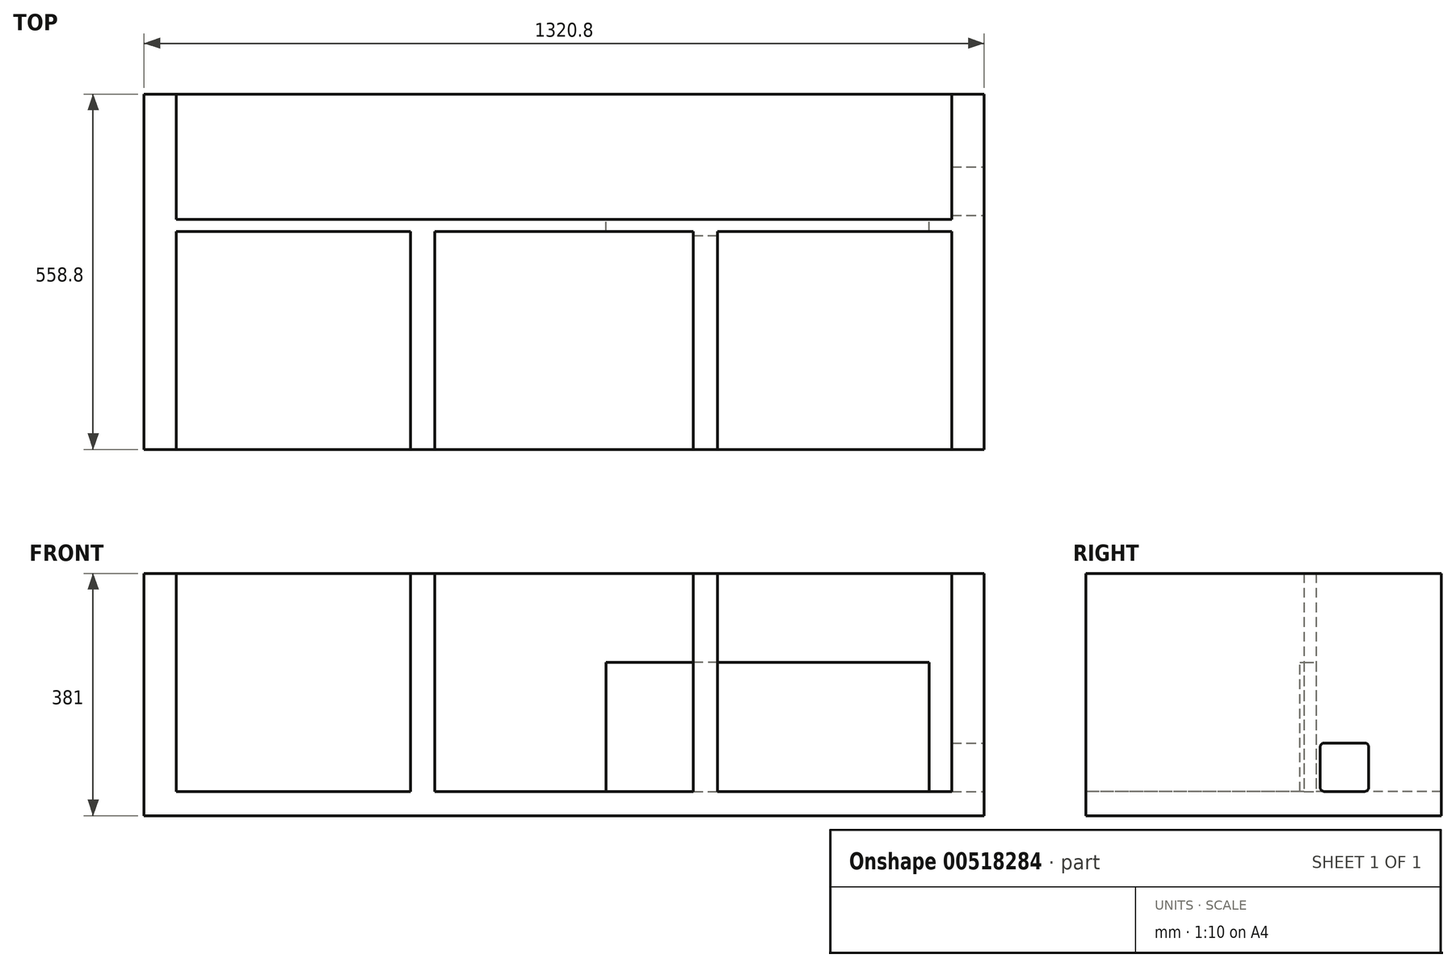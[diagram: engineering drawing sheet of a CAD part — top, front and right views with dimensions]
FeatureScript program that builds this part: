
annotation { "Feature Type Name" : "Feature", "Feature Type Description" : "" }
export const myFeature = defineFeature(function(context is Context, id is Id, definition is map)
    precondition{}
    {
        {
            var Q0;
            Q0=qCreatedBy(makeId("Top.planeOp"),FACE);
            var sketch = newSketch(context, id + "F0", { "sketchPlane" : qUnion([Q0])});
            skLineSegment(sketch, "E0.bottom", {"start": v(-660.38, -103.16) * mm, "end": v(660.42, -103.16) * mm});
            skLineSegment(sketch, "E0.top", {"start": v(-660.38, -661.96) * mm, "end": v(660.42, -661.96) * mm});
            skLineSegment(sketch, "E0.left", {"start": v(-660.38, -103.16) * mm, "end": v(-660.38, -661.96) * mm});
            skLineSegment(sketch, "E0.right", {"start": v(660.42, -103.16) * mm, "end": v(660.42, -661.96) * mm});
            skSolve(sketch);
        }
        {
            var Q0;
            Q0=makeQuery(id+"F0.imprint","IMPRINT",FACE,{"disambiguationData":[TD([[makeQuery(id+"F0.imprint","IMPRINT",EDGE,{"derivedFrom":sQuery(id+"F0.wireOp",EDGE,"E0.bottom")}),-1.0]])]});
            extrude(context, id + "F1", {"entities" : qUnion([Q0]), "depth" : 38.1 * mm, "offsetDistance" : 25.4 * mm});
        }
        {
            var Q0;
            Q0=makeQuery(id+"F1.opExtrude","CAP_FACE",FACE,{"disambiguationData":[OSD([sQuery(id+"F0.wireOp",EDGE,"E0.bottom"),sQuery(id+"F0.wireOp",EDGE,"E0.top"),sQuery(id+"F0.wireOp",EDGE,"E0.left"),sQuery(id+"F0.wireOp",EDGE,"E0.right")])],"isStart":false});
            var sketch = newSketch(context, id + "F2", { "sketchPlane" : qUnion([Q0])});
            skLineSegment(sketch, "E1.bottom", {"start": v(-660.38, -103.16) * mm, "end": v(-609.58, -103.16) * mm});
            skLineSegment(sketch, "E1.top", {"start": v(-660.38, -661.96) * mm, "end": v(-609.58, -661.96) * mm});
            skLineSegment(sketch, "E1.left", {"start": v(-660.38, -103.16) * mm, "end": v(-660.38, -661.96) * mm});
            skLineSegment(sketch, "E1.right", {"start": v(-609.58, -103.16) * mm, "end": v(-609.58, -661.96) * mm});
            skLineSegment(sketch, "E2.bottom", {"start": v(660.42, -103.16) * mm, "end": v(609.62, -103.16) * mm});
            skLineSegment(sketch, "E2.top", {"start": v(660.42, -661.96) * mm, "end": v(609.62, -661.96) * mm});
            skLineSegment(sketch, "E2.left", {"start": v(660.42, -103.16) * mm, "end": v(660.42, -661.96) * mm});
            skLineSegment(sketch, "E2.right", {"start": v(609.62, -103.16) * mm, "end": v(609.62, -661.96) * mm});
            skLineSegment(sketch, "E3.bottom", {"start": v(-609.58, -300.01) * mm, "end": v(609.62, -300.01) * mm});
            skLineSegment(sketch, "E3.top", {"start": v(-609.58, -319.06) * mm, "end": v(609.62, -319.06) * mm});
            skLineSegment(sketch, "E3.left", {"start": v(-609.58, -300.01) * mm, "end": v(-609.58, -319.06) * mm});
            skLineSegment(sketch, "E3.right", {"start": v(609.62, -300.01) * mm, "end": v(609.62, -319.06) * mm});
            skLineSegment(sketch, "E4.bottom", {"start": v(-241.28, -319.06) * mm, "end": v(-203.18, -319.06) * mm});
            skLineSegment(sketch, "E4.top", {"start": v(-241.28, -661.96) * mm, "end": v(-203.18, -661.96) * mm});
            skLineSegment(sketch, "E4.left", {"start": v(-241.28, -319.06) * mm, "end": v(-241.28, -661.96) * mm});
            skLineSegment(sketch, "E4.right", {"start": v(-203.18, -319.06) * mm, "end": v(-203.18, -661.96) * mm});
            skLineSegment(sketch, "E5.bottom", {"start": v(203.22, -319.06) * mm, "end": v(241.32, -319.06) * mm});
            skLineSegment(sketch, "E5.top", {"start": v(203.22, -661.96) * mm, "end": v(241.32, -661.96) * mm});
            skLineSegment(sketch, "E5.left", {"start": v(203.22, -319.06) * mm, "end": v(203.22, -661.96) * mm});
            skLineSegment(sketch, "E5.right", {"start": v(241.32, -319.06) * mm, "end": v(241.32, -661.96) * mm});
            skSolve(sketch);
        }
        {
            var Q0;
            Q0 = qSketchRegion(id + "F2", true);
            extrude(context, id + "F3", {"entities" : qUnion([Q0]), "operationType" : NewBodyOperationType.ADD, "depth" : 342.9 * mm, "offsetDistance" : 25.4 * mm});
        }
        {
            var Q0;
            Q0=makeQuery(id+"F3.boolean.opBoolean","MERGE",FACE,{"derivedFrom":[makeQuery(id+"F1.opExtrude","SWEPT_FACE",FACE,{"disambiguationData":[OSD([sQuery(id+"F0.wireOp",EDGE,"E0.right")])]}),makeQuery(id+"F3.opExtrude","SWEPT_FACE",FACE,{"disambiguationData":[OSD([sQuery(id+"F2.wireOp",EDGE,"E2.left")])]})]});
            var sketch = newSketch(context, id + "F4", { "sketchPlane" : qUnion([Q0])});
            skLineSegment(sketch, "E6.bottom", {"start": v(-287.31, 114.3) * mm, "end": v(-223.81, 114.3) * mm});
            skLineSegment(sketch, "E6.top", {"start": v(-287.31, 38.1) * mm, "end": v(-223.81, 38.1) * mm});
            skLineSegment(sketch, "E6.left", {"start": v(-293.66, 107.95) * mm, "end": v(-293.66, 44.45) * mm});
            skLineSegment(sketch, "E6.right", {"start": v(-217.46, 107.95) * mm, "end": v(-217.46, 44.45) * mm});
            skPoint(sketch, "E7.visualSharp", {"position": v(-293.66, 38.1) * mm});
            skArc(sketch, "E7.filletArc", {"start": v(-293.66, 44.45) * mm, "mid": v(-291.8, 39.96) * mm, "end": v(-287.31, 38.1) * mm});
            skPoint(sketch, "E8.visualSharp", {"position": v(-293.66, 114.3) * mm});
            skArc(sketch, "E8.filletArc", {"start": v(-287.31, 114.3) * mm, "mid": v(-291.8, 112.44) * mm, "end": v(-293.66, 107.95) * mm});
            skPoint(sketch, "E9.visualSharp", {"position": v(-217.46, 114.3) * mm});
            skArc(sketch, "E9.filletArc", {"start": v(-217.46, 107.95) * mm, "mid": v(-219.32, 112.44) * mm, "end": v(-223.81, 114.3) * mm});
            skPoint(sketch, "E10.visualSharp", {"position": v(-217.46, 38.1) * mm});
            skArc(sketch, "E10.filletArc", {"start": v(-223.81, 38.1) * mm, "mid": v(-219.32, 39.96) * mm, "end": v(-217.46, 44.45) * mm});
            skSolve(sketch);
        }
        {
            var Q0;
            Q0=makeQuery(id+"F4.imprint","IMPRINT",FACE,{"disambiguationData":[TD([[makeQuery(id+"F4.imprint","IMPRINT",EDGE,{"derivedFrom":sQuery(id+"F4.wireOp",EDGE,"E6.bottom")}),-1.0]])]});
            extrude(context, id + "F5", {"entities" : qUnion([Q0]), "operationType" : NewBodyOperationType.REMOVE, "oppositeDirection" : true, "depth" : 148.84 * mm, "offsetDistance" : 25.4 * mm});
        }
        {
            var Q0;
            Q0=makeQuery(id+"F3.opExtrude","SWEPT_FACE",FACE,{"disambiguationData":[OSD([sQuery(id+"F2.wireOp",EDGE,"E3.bottom")])]});
            var sketch = newSketch(context, id + "F6", { "sketchPlane" : qUnion([Q0])});
            skLineSegment(sketch, "E11.bottom", {"start": v(-574.03, 241.3) * mm, "end": v(-66.03, 241.3) * mm});
            skLineSegment(sketch, "E11.top", {"start": v(-574.03, 38.1) * mm, "end": v(-66.03, 38.1) * mm});
            skLineSegment(sketch, "E11.left", {"start": v(-574.03, 241.3) * mm, "end": v(-574.03, 38.1) * mm});
            skLineSegment(sketch, "E11.right", {"start": v(-66.03, 241.3) * mm, "end": v(-66.03, 38.1) * mm});
            skSolve(sketch);
        }
        {
            var Q0;
            Q0=makeQuery(id+"F6.imprint","IMPRINT",FACE,{"disambiguationData":[TD([[makeQuery(id+"F6.imprint","IMPRINT",EDGE,{"derivedFrom":sQuery(id+"F6.wireOp",EDGE,"E11.bottom")}),-1.0]])]});
            extrude(context, id + "F7", {"entities" : qUnion([Q0]), "operationType" : NewBodyOperationType.REMOVE, "oppositeDirection" : true, "depth" : 25.4 * mm, "offsetDistance" : 25.4 * mm});
        }
    });
